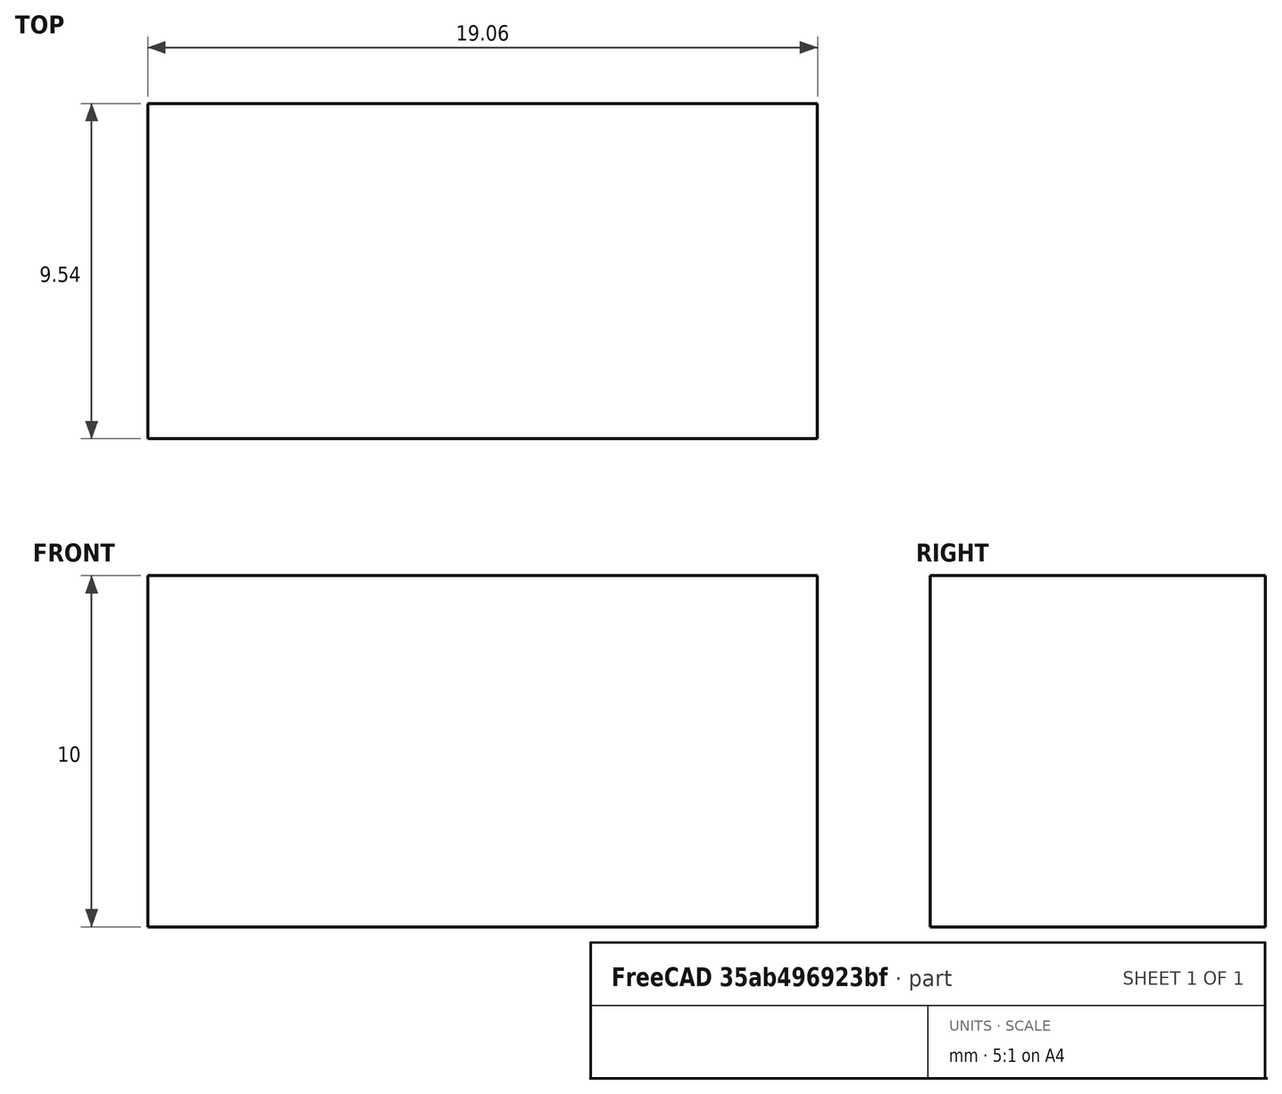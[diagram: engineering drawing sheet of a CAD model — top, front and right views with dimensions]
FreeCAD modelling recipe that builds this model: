
FCSTD DOCUMENT  (FreeCAD 0.21R38998 (Git))
Label: waveguide3
License: All rights reserved
LicenseURL: https://en.wikipedia.org/wiki/All_rights_reserved
objects: PartDesign::Body×2, Sketcher::SketchObject×1, PartDesign::Pad×1, PartDesign::SubShapeBinder×1, App::Part×1
note: 8 computed .brp shape members not serialized (recipe doc carries the construction recipe); baked Part::Feature solids carry a one-line shape summary decoded from their .brp

FEATURE [Sketcher::SketchObject] Sketch
  ArcFitTolerance = 1e-06
  AttachmentSupport = -> [XZ_Plane]
  ExternalBSplineMaxDegree = 5
  ExternalBSplineTolerance = 0.0001
  FixShape = 1
  FullyConstrained = true
  InternalTolerance = 1e-06
  InvalidShape = false
  MakeInternals = false
  MapMode = 5
  Placement = pos=(0,0,0) rot=(1,0,0;1.5708rad)
  Support = -> [XZ_Plane]
  TreeRank = 14
  ValidateShape = false
  sketch-geometry (4):
    g0: LineSegment StartX=-9.525 StartY=5 StartZ=0 EndX=9.525 EndY=5 EndZ=0
    g1: LineSegment StartX=9.525 StartY=5 StartZ=0 EndX=9.525 EndY=-5 EndZ=0
    g2: LineSegment StartX=9.525 StartY=-5 StartZ=0 EndX=-9.525 EndY=-5 EndZ=0
    g3: LineSegment StartX=-9.525 StartY=-5 StartZ=0 EndX=-9.525 EndY=5 EndZ=0
  constraints (11):
    c: Coincident(g0,g1)
    c: Coincident(g1,g2)
    c: Coincident(g2,g3)
    c: Coincident(g3,g0)
    c: Horizontal(g0)
    c: Horizontal(g2)
    c: Vertical(g1)
    c: DistanceY(g3,g3) = 10
    c: DistanceX(g2,g2) = 19.05
    c: Vertical(g3)
    c: Symmetric(g0,g2,g-1)
FEATURE [PartDesign::Pad] Pad
  AddSubType = 0
  AlongSketchNormal = false
  AutoTaperInnerAngle = true
  CheckUpToFaceLimits = true
  ClaimChildren = false
  Direction = (0,-1,0)
  Fit = 0
  FitJoin = 0
  FixShape = 1
  InnerFit = 0
  InnerFitJoin = 0
  InvalidShape = false
  Length = 9.54
  Length2 = 10
  Linearize = true
  NewSolid = false
  Profile = -> Sketch
  ReferenceAxis = -> Sketch [N_Axis]
  Suppress = false
  TaperInnerAngle = 0
  TaperInnerAngleRev = 0
  TreeRank = 15
  Type = 0
  ValidateShape = true
  _ProfileBasedVersion = 1
FEATURE [PartDesign::Body] Body  label="DIEL_CAVITY"
  AutoGroupSolids = false
  ClaimAllChildren = false
  ExportMode = 0
  FixShape = 1
  Group = -> [Sketch,Pad]
  InvalidShape = false
  Origin = -> Origin001
  Tip = -> Pad
  TreeRank = 13
  ValidateShape = false
  _ExportChildren = -> [Pad]
  _GroupVersion = 1
FEATURE [PartDesign::SubShapeBinder] Binder  label="Binder(Pad)"
  BindCopyOnChange = 0
  BindMode = 0
  ClaimChildren = false
  Context = -> Part [Body001.Binder.]
  EdgeTolerance = 1e-06
  FillStyle = 0
  FixShape = 1
  Fuse = false
  Group_EnableExport = true
  InvalidShape = false
  MakeFace = true
  MergeEdges = true
  OffsetFill = false
  OffsetIntersection = false
  OffsetJoinType = 0
  OffsetOpenResult = false
  Outline = false
  PartialLoad = false
  Relative = true
  SplitEdges = false
  Support = -> [Body[Pad.Face1]]
  TightBound = false
  TreeRank = 26
  ValidateShape = false
  _Version = 8
FEATURE [PartDesign::Body] Body001  label="WGP_1"
  AutoGroupSolids = false
  ClaimAllChildren = false
  ExportMode = 2
  FixShape = 1
  Group = -> [Binder]
  InvalidShape = false
  Origin = -> Origin002
  TreeRank = 25
  ValidateShape = false
  _ExportChildren = -> [Binder]
  _GroupVersion = 1
FEATURE [App::Part] Part  label="CMP_waveguide3"
  ClaimAllChildren = false
  ExportMode = 1
  Group = -> [Body,Body001]
  Origin = -> Origin
  TreeRank = 3
  _ExportChildren = -> [Body,Body001]
  _GroupVersion = 1
